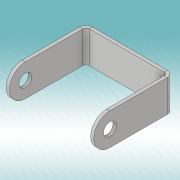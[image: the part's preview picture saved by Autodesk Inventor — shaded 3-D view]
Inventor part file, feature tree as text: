
AUTODESK INVENTOR PART (.ipt)
format: ipt  version: 2019 (Build 230136000, 136)  size: 181,248 bytes
history: native  units: in
note: dims shown in document units (in); Inventor stores cm internally (conversion verified against a paired STEP export)
features: sheet_metal_op x6, sketch x6, other x4, extrude x2
ambient origin geometry x8: Origin, YZ Plane, XZ Plane, XY Plane, X Axis, Y Axis, Z Axis, Center Point
bodies: Solid1 (feature_tree)
feature tree (18):
  extrude  "Extrusion1"  Depth=0.0787in TaperAngle=0.0deg
  sheet_metal_op  "Flange1"
  sheet_metal_op  "Flange2"
  extrude  "Extrusion2"  Depth=0.0787in
  sketch  "Sketch1"  dims[d0=1.0827in d4=0.0787in d5=0.0in]
  sketch  "Sketch2"  dims[d6=0.7874in d7=0.0787in]
  other  "Plate1"
  sheet_metal_op  "Bend1"
  sheet_metal_op  "Corner1"
  sketch  "Sketch3"  dims[d8=0.0787in]
  other  "Plate2"
  sheet_metal_op  "Bend2"
  sheet_metal_op  "Corner2"
  sketch  "Sketch5"  dims[d9=0.0394in]
  sketch  "Sketch6"  dims[d10=0.1575in]
  sketch  "Sketch7"  dims[d11=0.0787in d12=1.9685in d13=90.0deg d14=0.0787in d15=0.315in d16=0.0787in d17=0.0787in d18=0.0787in d19=0.0394in d20=0.1575in d21=0.0787in d22=1.9685in d23=90.0deg d24=0.0787in d25=0.315in d26=0.0787in d27=0.0787in d38=0.3937in d39=0.3937in d40=0.3937in d41=0.0787in d42=0.0in d43=0.3937in d44=0.0787in d45=0.0in d46=0.315in d47=0.315in d48=0.3937in d49=0.3543in d51=0.0039in d52=0.0in d53=0.9252in]
  other  "Cut1"
  other  "Cut2"
